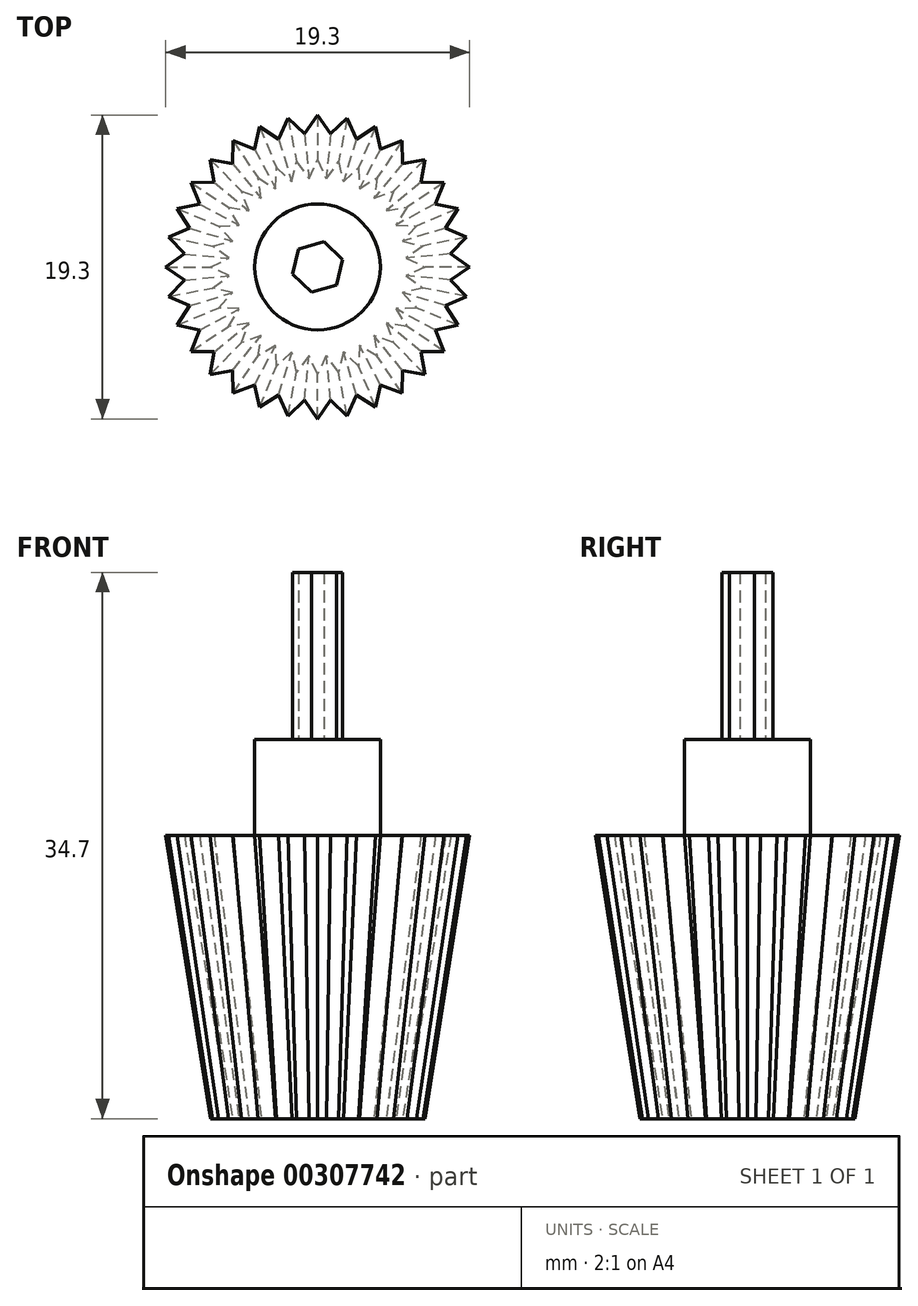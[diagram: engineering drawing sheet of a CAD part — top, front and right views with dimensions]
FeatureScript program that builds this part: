
annotation { "Feature Type Name" : "Feature", "Feature Type Description" : "" }
export const myFeature = defineFeature(function(context is Context, id is Id, definition is map)
    precondition{}
    {
        {
            var Q0;
            Q0=qCreatedBy(makeId("Top.planeOp"),FACE);
            var sketch = newSketch(context, id + "F0", { "sketchPlane" : qUnion([Q0])});
            skCircle(sketch, "E0", {"center": v(0, 0) * mm, "radius": 8.5 * mm});
            skSolve(sketch);
        }
        {
            var Q0;
            Q0=makeQuery(id+"F0.imprint","IMPRINT",FACE,{"disambiguationData":[TD([[makeQuery(id+"F0.imprint","IMPRINT",EDGE,{"derivedFrom":sQuery(id+"F0.wireOp",EDGE,"E0")}),1.0]])]});
            extrude(context, id + "F1", {"entities" : qUnion([Q0]), "oppositeDirection" : true, "depth" : 18 * mm, "hasDraft" : true, "draftAngle" : 9 * degree, "draftPullDirection" : true});
        }
        {
            var Q0;
            Q0=makeQuery(id+"F1.opExtrude","CAP_FACE",FACE,{"disambiguationData":[OSD([sQuery(id+"F0.wireOp",EDGE,"E0")])],"isStart":true});
            var sketch = newSketch(context, id + "F2", { "sketchPlane" : qUnion([Q0])});
            skPoint(sketch, "E1.end.orphan", {"position": v(0, -4.4) * mm});
            skLineSegment(sketch, "E2", {"start": v(0, 9.65) * mm, "end": v(-0.83, 8.46) * mm});
            skLineSegment(sketch, "E3", {"start": v(-0.83, 8.46) * mm, "end": v(0.83, 8.46) * mm});
            skLineSegment(sketch, "E4", {"start": v(0.83, 8.46) * mm, "end": v(0, 9.65) * mm});
            skSolve(sketch);
        }
        {
            var Q0;
            Q0=makeQuery(id+"F1.opExtrude","CAP_FACE",FACE,{"disambiguationData":[OSD([sQuery(id+"F0.wireOp",EDGE,"E0")])],"isStart":false});
            var sketch = newSketch(context, id + "F3", { "sketchPlane" : qUnion([Q0])});
            skPoint(sketch, "E5.start.orphan", {"position": v(0, -9.67) * mm});
            skLineSegment(sketch, "E6", {"start": v(0, -6.81) * mm, "end": v(0.55, -5.62) * mm});
            skLineSegment(sketch, "E7", {"start": v(0.55, -5.62) * mm, "end": v(-0.55, -5.62) * mm});
            skLineSegment(sketch, "E8", {"start": v(-0.55, -5.62) * mm, "end": v(0, -6.81) * mm});
            skSolve(sketch);
        }
        {
            var Q1;
            {var subQ0=sQuery(id+"F2.wireOp",EDGE,"E2");Q1=makeQuery(id+"F2.imprint","IMPRINT",FACE,{"disambiguationData":[TD([[makeQuery(id+"F2.imprint","IMPRINT",EDGE,{"derivedFrom":subQ0}),1.0]])]});}
            var Q2;
            {var subQ0=sQuery(id+"F3.wireOp",EDGE,"E6");Q2=makeQuery(id+"F3.imprint","IMPRINT",FACE,{"disambiguationData":[TD([[makeQuery(id+"F3.imprint","IMPRINT",EDGE,{"derivedFrom":subQ0}),1.0]])]});}
            loft(context, id + "F4", {"sheetProfilesArray" : [{ "sheetProfileEntities" : qUnion([Q1]) }, { "sheetProfileEntities" : qUnion([Q2]) }]});
        }
        {
            var Q0;
            Q0=qCreatedBy(makeId("Front.planeOp"),FACE);
            var sketch = newSketch(context, id + "F5", { "sketchPlane" : qUnion([Q0])});
            skLineSegment(sketch, "E9", {"start": v(0, 47.59) * mm, "end": v(0, -24.93) * mm, "construction": true});
            skSolve(sketch);
        }
        {
            var Q0;
            {var subQ0=sQuery(id+"F3.wireOp",EDGE,"E6");var subQ5=sQuery(id+"F2.wireOp",EDGE,"E2");Q0=makeQuery(id+"F4.opLoft","SWEPT_BODY",BODY,{"disambiguationData":[OSD([makeQuery(id+"F2.imprint","IMPRINT",FACE,{"disambiguationData":[TD([[makeQuery(id+"F2.imprint","IMPRINT",EDGE,{"derivedFrom":subQ5}),1.0]])]}),makeQuery(id+"F3.imprint","IMPRINT",FACE,{"disambiguationData":[TD([[makeQuery(id+"F3.imprint","IMPRINT",EDGE,{"derivedFrom":subQ0}),1.0]])]})])]});}
            var Q1;
            Q1=sQuery(id+"F5.wireOp",EDGE,"E9");
            circularPattern(context, id + "F6", {"operationType" : NewBodyOperationType.ADD, "entities" : qUnion([Q0]), "axis" : qUnion([Q1]), "angle" : 360 * degree, "instanceCount" : 32, "equalSpace" : true});
        }
        {
            var Q0;
            {var subQ0=sQuery(id+"F2.wireOp",EDGE,"E2");var subQ3=sQuery(id+"F0.wireOp",EDGE,"E0");var subQ5=makeQuery(id+"F4.opLoft","CAP_FACE",FACE,{"disambiguationData":[OSD([makeQuery(id+"F2.imprint","IMPRINT",FACE,{"disambiguationData":[TD([[makeQuery(id+"F2.imprint","IMPRINT",EDGE,{"derivedFrom":subQ0}),1.0]])]})])],"isStart":true});Q0=makeQuery(id+"F6.boolean.opBoolean","MERGE",FACE,{"derivedFrom":[makeQuery(id+"F1.opExtrude","CAP_FACE",FACE,{"disambiguationData":[OSD([subQ3])],"isStart":true}),subQ5,makeQuery(id+"F6.opPattern","COPY",FACE,{"derivedFrom":subQ5,"instanceName":"1"}),makeQuery(id+"F6.opPattern","COPY",FACE,{"derivedFrom":subQ5,"instanceName":"2"}),makeQuery(id+"F6.opPattern","COPY",FACE,{"derivedFrom":subQ5,"instanceName":"3"}),makeQuery(id+"F6.opPattern","COPY",FACE,{"derivedFrom":subQ5,"instanceName":"4"}),makeQuery(id+"F6.opPattern","COPY",FACE,{"derivedFrom":subQ5,"instanceName":"5"}),makeQuery(id+"F6.opPattern","COPY",FACE,{"derivedFrom":subQ5,"instanceName":"6"}),makeQuery(id+"F6.opPattern","COPY",FACE,{"derivedFrom":subQ5,"instanceName":"7"}),makeQuery(id+"F6.opPattern","COPY",FACE,{"derivedFrom":subQ5,"instanceName":"8"}),makeQuery(id+"F6.opPattern","COPY",FACE,{"derivedFrom":subQ5,"instanceName":"9"}),makeQuery(id+"F6.opPattern","COPY",FACE,{"derivedFrom":subQ5,"instanceName":"10"}),makeQuery(id+"F6.opPattern","COPY",FACE,{"derivedFrom":subQ5,"instanceName":"11"}),makeQuery(id+"F6.opPattern","COPY",FACE,{"derivedFrom":subQ5,"instanceName":"12"}),makeQuery(id+"F6.opPattern","COPY",FACE,{"derivedFrom":subQ5,"instanceName":"13"}),makeQuery(id+"F6.opPattern","COPY",FACE,{"derivedFrom":subQ5,"instanceName":"14"}),makeQuery(id+"F6.opPattern","COPY",FACE,{"derivedFrom":subQ5,"instanceName":"15"}),makeQuery(id+"F6.opPattern","COPY",FACE,{"derivedFrom":subQ5,"instanceName":"16"}),makeQuery(id+"F6.opPattern","COPY",FACE,{"derivedFrom":subQ5,"instanceName":"17"}),makeQuery(id+"F6.opPattern","COPY",FACE,{"derivedFrom":subQ5,"instanceName":"18"}),makeQuery(id+"F6.opPattern","COPY",FACE,{"derivedFrom":subQ5,"instanceName":"19"}),makeQuery(id+"F6.opPattern","COPY",FACE,{"derivedFrom":subQ5,"instanceName":"20"}),makeQuery(id+"F6.opPattern","COPY",FACE,{"derivedFrom":subQ5,"instanceName":"21"}),makeQuery(id+"F6.opPattern","COPY",FACE,{"derivedFrom":subQ5,"instanceName":"22"}),makeQuery(id+"F6.opPattern","COPY",FACE,{"derivedFrom":subQ5,"instanceName":"23"}),makeQuery(id+"F6.opPattern","COPY",FACE,{"derivedFrom":subQ5,"instanceName":"24"}),makeQuery(id+"F6.opPattern","COPY",FACE,{"derivedFrom":subQ5,"instanceName":"25"}),makeQuery(id+"F6.opPattern","COPY",FACE,{"derivedFrom":subQ5,"instanceName":"26"}),makeQuery(id+"F6.opPattern","COPY",FACE,{"derivedFrom":subQ5,"instanceName":"27"}),makeQuery(id+"F6.opPattern","COPY",FACE,{"derivedFrom":subQ5,"instanceName":"28"}),makeQuery(id+"F6.opPattern","COPY",FACE,{"derivedFrom":subQ5,"instanceName":"29"}),makeQuery(id+"F6.opPattern","COPY",FACE,{"derivedFrom":subQ5,"instanceName":"30"}),makeQuery(id+"F6.opPattern","COPY",FACE,{"derivedFrom":subQ5,"instanceName":"31"})]});}
            var sketch = newSketch(context, id + "F7", { "sketchPlane" : qUnion([Q0])});
            skCircle(sketch, "E10", {"center": v(0, 0) * mm, "radius": 4 * mm});
            skSolve(sketch);
        }
        {
            var Q0;
            Q0=makeQuery(id+"F7.imprint","IMPRINT",FACE,{"disambiguationData":[TD([[makeQuery(id+"F7.imprint","IMPRINT",EDGE,{"derivedFrom":sQuery(id+"F7.wireOp",EDGE,"E10")}),1.0]])]});
            extrude(context, id + "F8", {"entities" : qUnion([Q0]), "operationType" : NewBodyOperationType.ADD, "depth" : 6.1 * mm});
        }
        {
            var Q0;
            Q0=makeQuery(id+"F8.opExtrude","CAP_FACE",FACE,{"disambiguationData":[OSD([sQuery(id+"F7.wireOp",EDGE,"E10")])],"isStart":false});
            var sketch = newSketch(context, id + "F9", { "sketchPlane" : qUnion([Q0])});
            skCircle(sketch, "E11.cCircle", {"center": v(0, 0) * mm, "radius": 1.44 * mm, "construction": true});
            skLineSegment(sketch, "E11.0", {"start": v(-1.6, -0.46) * mm, "end": v(-1.2, 1.15) * mm});
            skLineSegment(sketch, "E11.1", {"start": v(-1.2, 1.15) * mm, "end": v(0.4, 1.6) * mm});
            skLineSegment(sketch, "E11.2", {"start": v(0.4, 1.6) * mm, "end": v(1.6, 0.46) * mm});
            skLineSegment(sketch, "E11.3", {"start": v(1.6, 0.46) * mm, "end": v(1.2, -1.15) * mm});
            skLineSegment(sketch, "E11.4", {"start": v(1.2, -1.15) * mm, "end": v(-0.4, -1.6) * mm});
            skLineSegment(sketch, "E11.5", {"start": v(-0.4, -1.6) * mm, "end": v(-1.6, -0.46) * mm});
            skPoint(sketch, "E11.0.midPoint", {"position": v(-1.4, 0.34) * mm});
            skSolve(sketch);
        }
        {
            var Q0;
            Q0 = qSketchRegion(id + "F9", true);
            extrude(context, id + "F10", {"entities" : qUnion([Q0]), "operationType" : NewBodyOperationType.ADD, "depth" : 10.6 * mm});
        }
    });
